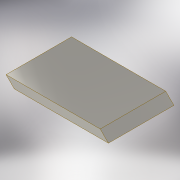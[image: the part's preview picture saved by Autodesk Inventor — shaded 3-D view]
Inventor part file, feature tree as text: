
AUTODESK INVENTOR PART (.ipt)
format: ipt  version: 2020 (Build 240168000, 168)  size: 119,296 bytes
history: native  units: in
note: dims shown in document units (in); Inventor stores cm internally (conversion verified against a paired STEP export)
features: extrude x2, chamfer x2, sketch x2
ambient origin geometry x8: Origin, YZ Plane, XZ Plane, XY Plane, X Axis, Y Axis, Z Axis, Center Point
bodies: Solid1 (feature_tree)
feature tree (6):
  extrude  "Extrusion1"  Depth=6.2992in
  chamfer  "Chamfer1"  Distance=0.7874in
  extrude  "Extrusion2"  Depth=0.7874in TaperAngle=0.0deg
  chamfer  "Chamfer2"  Distance=0.7874in Angle=45.0deg
  sketch  "Sketch1"  dims[d0=9.0551in d1=6.2992in d2=0.7874in d3=0.0in]
  sketch  "Sketch2"  dims[d4=0.7874in d5=0.0787in d6=45.0deg d7=0.7874in d8=0.0in d9=0.7874in d10=0.0787in d11=45.0deg]
